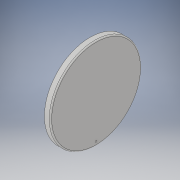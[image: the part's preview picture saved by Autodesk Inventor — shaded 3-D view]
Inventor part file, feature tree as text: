
AUTODESK INVENTOR PART (.ipt)
format: ipt  version: 2019 (Build 230136000, 136)  size: 137,728 bytes
history: native  units: in
note: dims shown in document units (in); Inventor stores cm internally (conversion verified against a paired STEP export)
features: sketch x3, hole x2, revolve x1, fillet x1, chamfer x1, projected_geometry x1
ambient origin geometry x8: Origin, YZ Plane, XZ Plane, XY Plane, X Axis, Y Axis, Z Axis, Center Point
bodies: Body1 (feature_tree)
feature tree (9):
  revolve  "Revolution1"  [1 undecoded]
  fillet  "Fillet1"  Radius=0.25in
  chamfer  "Chamfer1"  Distance=0.025in
  hole  "Hole1"  [1 undecoded]
  hole  "Hole2"  [1 undecoded]
  sketch  "Sketch5"  dims[d9=0.125in d10=1.875in d14=0.25in]
  sketch  "Sketch6"  dims[d15=90.0deg]
  projected_geometry  "Projected Loop2"
  sketch  "Sketch7"  dims[d17=0.05in d18=0.025in d19=0.165in d21=0.225in d22=0.025in d23=0.125in d24=45.0deg d27=1.7in d29=0.06in d30=0.75in d31=0.375in d32=0.25in d33=0.5635in d34=1.0in d35=0.8108in d36=0.104in d37=0.276in d38=0.375in d39=0.25in d40=0.5635in d41=0.432in d42=0.8108in d43=2.75in d44=0.75in]
note: 3 required parameter values undecoded (feature->parameter linkage not recoverable at this tier; creation-order binding heuristic only, values carry confidence <= 0.55)